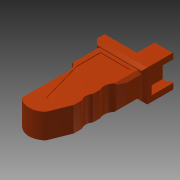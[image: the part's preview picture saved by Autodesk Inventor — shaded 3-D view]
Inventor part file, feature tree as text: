
AUTODESK INVENTOR PART (.ipt)
format: ipt  version: 2013 (Build 170138000, 138)  size: 339,968 bytes
history: native  units: mm
features: extrude x19, sketch x19, chamfer x4, fillet x2
ambient origin geometry x8: Origin, YZ Plane, XZ Plane, XY Plane, X Axis, Y Axis, Z Axis, Center Point
bodies: Solid1 (feature_tree)
feature tree (44):
  extrude  "Extrusion1"  Depth=34.324mm
  extrude  "Extrusion2"  Depth=3.53mm
  extrude  "Extrusion3"  Depth=2.0mm
  extrude  "Extrusion4"  Depth=5.0mm TaperAngle=0.0deg
  extrude  "Extrusion5"  Depth=5.0mm TaperAngle=0.0deg
  extrude  "Extrusion6"  Depth=10.0mm TaperAngle=0.0deg
  extrude  "Extrusion7"  Depth=5.0mm
  extrude  "Extrusion8"  Depth=5.0mm
  extrude  "Extrusion9"  Depth=5.0mm TaperAngle=0.0deg
  extrude  "Extrusion10"  Depth=3.53mm
  chamfer  "Chamfer1"  Distance=0.5mm
  extrude  "Extrusion11"  Depth=5.0mm
  extrude  "Extrusion12"  Depth=5.0mm
  extrude  "Extrusion13"  Depth=5.0mm
  extrude  "Extrusion14"  Depth=3.0mm TaperAngle=45.0deg
  chamfer  "Chamfer2"  Distance=4.0mm Angle=45.0deg
  chamfer  "Chamfer3"  Distance=34.324mm
  extrude  "Extrusion15"  Depth=4.0mm
  chamfer  "Chamfer4"  Distance=2.0mm
  fillet  "Fillet1"  Radius=2.0mm
  extrude  "Extrusion16"  Depth=5.0mm
  extrude  "Extrusion17"  Depth=1.0mm TaperAngle=0.0deg
  extrude  "Extrusion18"  Depth=5.0mm
  extrude  "Extrusion19"  Depth=1.0mm TaperAngle=0.0deg
  fillet  "Fillet2"  Radius=5.0mm
  sketch  "Sketch1"  dims[d0=35.324mm d2=34.324mm]
  sketch  "Sketch2"  dims[d3=10.0mm d4=0.0mm d5=3.53mm]
  sketch  "Sketch3"  dims[d7=2.0mm d8=2.0mm]
  sketch  "Sketch4"  dims[d9=10.0mm d10=0.0mm d11=5.0mm d12=0.0mm]
  sketch  "Sketch5"  dims[d13=5.0mm d14=0.0mm d15=5.0mm d16=0.0mm]
  sketch  "Sketch6"  dims[d17=5.0mm d19=10.0mm d20=0.0mm]
  sketch  "Sketch7"  dims[d21=5.0mm d22=0.0mm d23=5.0mm]
  sketch  "Sketch8"  dims[d24=5.0mm d25=0.0mm d26=5.0mm]
  sketch  "Sketch9"  dims[d27=5.0mm d28=0.0mm d29=5.0mm d30=0.0mm]
  sketch  "Sketch10"  dims[d31=1.0mm d32=2.0mm d33=45.0deg d34=3.53mm d36=0.5mm d37=0.0mm]
  sketch  "Sketch11"  dims[d38=45.0mm d39=0.0mm d40=5.0mm]
  sketch  "Sketch12"  dims[d41=3.0mm d42=0.0mm d43=5.0mm]
  sketch  "Sketch13"  dims[d44=5.0mm d45=5.0mm]
  sketch  "Sketch14"  dims[d46=20.0mm d47=0.0mm d48=3.0mm d49=2.0mm d50=45.0deg d51=4.0mm d52=2.0mm d53=45.0deg d54=34.324mm d55=0.0mm]
  sketch  "Sketch15"  dims[d56=4.0mm d57=2.0mm d58=45.0deg d59=4.0mm d60=2.0mm d61=0.0mm d62=2.0mm d63=0.0mm]
  sketch  "Sketch16"  dims[d64=5.0mm d65=5.0mm]
  sketch  "Sketch17"  dims[d66=5.0mm d67=1.0mm d68=0.0mm]
  sketch  "Sketch18"  dims[d69=5.0mm d70=5.0mm]
  sketch  "Sketch19"  dims[d71=5.0mm d72=1.0mm d73=0.0mm d74=5.0mm]
